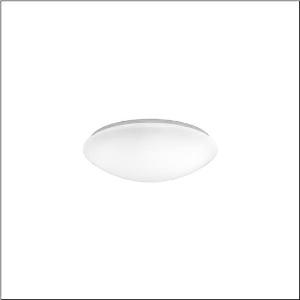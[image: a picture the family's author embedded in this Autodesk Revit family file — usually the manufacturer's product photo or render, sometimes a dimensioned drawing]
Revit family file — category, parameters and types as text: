
# Revit family: round_31_b_5pja030001a
name_source: partatom
category: Lighting Fixtures
units: mm (PartAtom-declared; Revit-internal decimal feet)

## family parameters
Cut with Voids When Loaded = No
Host = Face
Light Source = No
Part Type = Normal
Room Calculation Point = No
Round Connector Dimension = Use Diameter
Shared = No

## types (1)
- Round 31 B (1 x LED, 1900 lm, 15 W, 4000K)
    Apparent Load = 15 VA
    CIE Flux Codes = 42 71 89 88 100
    Color Rendering = 80
    Color Temperature = 4000K
    Default Elevation = 1800 mm
    Description = Round 31 B, wall and ceiling luminaire, primary optical cover: enclosure, of PMMA, light emission: direct distribution, primary light characteristic: symmetric, installation type: surface-mounted, LED, rated luminous flux: 1.900lm, luminous efficacy: 126lm/W, light colour: 840, colour temperature: 4000K, with terminal, 3-pole, max. 2.5mm², mains connection: 230V, AC, 50/60Hz, rated input power: 15W, luminaire housing, round, of steel, white, diameter: 290mm, height: 85mm, protection rating (complete): IP40, insulation class (complete): insulation class I (protective earthing), certification: CE, impact resistance: IK02, packaging unit: 1 piece
    Height = 85 mm
    Lamp = 1 x LED
    Lamp Light Flux = 1900 lm
    Lamp Power = 15 W
    Lamp count = 1
    Length = 290 mm
    Luminous efficacy = 127 lm/W
    Manufacturer = Siteco
    ModVariant = No
    Model = 5PJA030001A
    Mounting Place = Ceiling
    Mounting Type = Surface mounted
    Number of Poles = 1
    OnlyDefault = Yes
    Power Factor = 1
    Product Name = Round 31 B
    Product group = wall and ceiling luminaire
    ProductGroupID = 301
    Protection Class = Protection class I
    Protection Degree = IP 40
    RLX_Detail_Level = 1
    RLX_Emergency_Light_Flux = 0 lm
    RLX_Emergency_Type = 0
    RLX_Emergency_Type_DB = No
    RlxData = <blob elided: 9181 chars, md5=034209b7>
    Socket = socket
    Standby Power = 0 W
    System Light Flux = 1900 lm
    System Power = 15 W
    Type Comments = Product without accessories
    Type Image = l_1258346.jpg
    URL = http://relux.com
    VarID = ---
    Voltage = 0 V
    Weight = 0.00 kg
    Width = 0 mm  [stored 0 ft]

note: [stored X ft] marks values corroborated as IEEE doubles in the binary element streams (Revit-internal decimal feet)

## geometry (parser evidence)
native form markers: Sweep x12
no freeform markers — native parametric forms only
